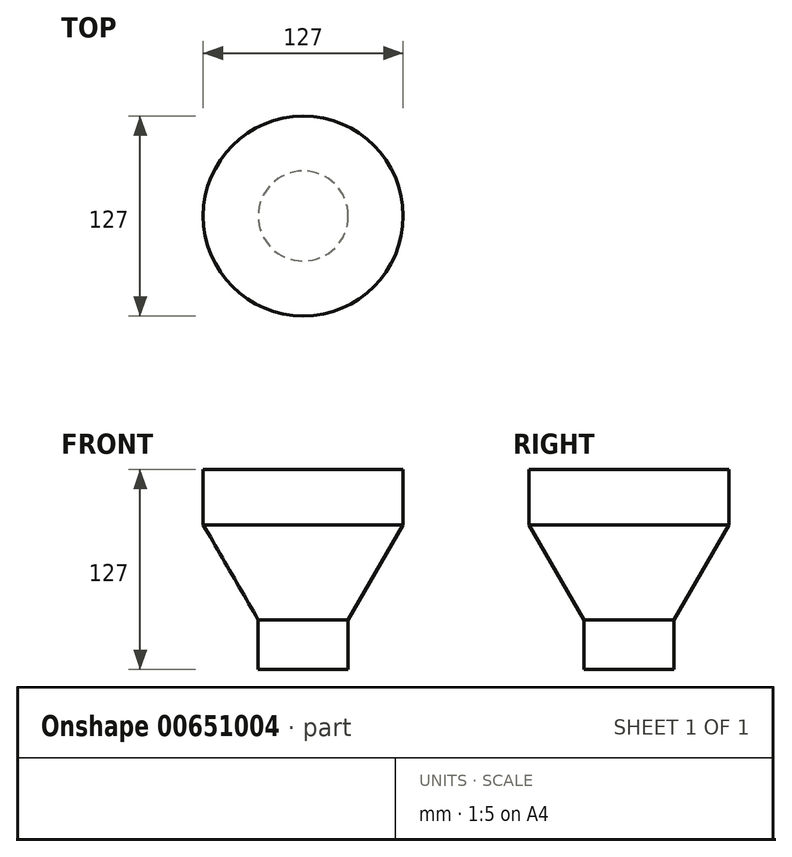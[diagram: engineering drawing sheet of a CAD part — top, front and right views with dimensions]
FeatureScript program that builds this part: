
annotation { "Feature Type Name" : "Feature", "Feature Type Description" : "" }
export const myFeature = defineFeature(function(context is Context, id is Id, definition is map)
    precondition{}
    {
        {
            var Q0;
            Q0=qCreatedBy(makeId("Front.planeOp"),FACE);
            var sketch = newSketch(context, id + "F0", { "sketchPlane" : qUnion([Q0])});
            skLineSegment(sketch, "E0", {"start": v(0, 0) * mm, "end": v(28.58, 0) * mm});
            skLineSegment(sketch, "E1", {"start": v(0, 0) * mm, "end": v(0, 127) * mm});
            skLineSegment(sketch, "E2", {"start": v(0, 127) * mm, "end": v(63.5, 127) * mm});
            skLineSegment(sketch, "E3", {"start": v(28.58, 0) * mm, "end": v(28.58, 31.46) * mm});
            skLineSegment(sketch, "E4", {"start": v(63.5, 127) * mm, "end": v(63.5, 91.93) * mm});
            skLineSegment(sketch, "E5", {"start": v(28.58, 31.46) * mm, "end": v(63.5, 91.93) * mm});
            skSolve(sketch);
        }
        {
            var Q0;
            Q0=makeQuery(id+"F0.imprint","IMPRINT",FACE,{"disambiguationData":[TD([[makeQuery(id+"F0.imprint","IMPRINT",EDGE,{"derivedFrom":sQuery(id+"F0.wireOp",EDGE,"E0")}),1.0]])]});
            var Q1;
            Q1=sQuery(id+"F0.wireOp",EDGE,"E1");
            revolve(context, id + "F1", {"entities" : qUnion([Q0]), "axis" : qUnion([Q1]), "revolveType" : RevolveType.FULL});
        }
    });
